# Revit family: Reece_Waste_Mizu_Drift_Tile Insert Waste
name_source: partatom
category: Plumbing Fixtures
revit_build: Autodesk Revit 2018 (Build: 20190510_1515(x64)
units: mm (PartAtom-declared; Revit-internal decimal feet)

## family parameters
Cut with Voids When Loaded = No
Host = Face
Part Type = Normal
Room Calculation Point = Yes
Round Connector Dimension = Use Diameter
Shared = Yes

## types (1)
- 100mm_Chrome
    CW Connection = No
    CWFU = 0
    Default Elevation = 1000 mm  [stored 3.28084 ft]
    Description = Mizu Drift Tile Insert Waste 100mm Chrome
    Disclaimer = THIS FILE IS THE PROPERTY OF THE REECE GROUP. IT MAY NOT BE REPRODUCED, REVERSE-ENGINEERED OR MODIFIED. ANY REPUBLICATION, TRANSMISSION OR DISTRIBUTION FOR THE PURPOSE OF COMMERCIALLY EXPLOITING THE FILES IS PROHIBITED.
    HW Connection = No
    HWFU = 0
    Keynote = Product #202209, Reece_Waste_Mizu_Drift_Tile Insert Waste - 100mm_Chrome
    Manufacturer = Mizu
    Model = Drift
    Reece_Detail_Disclaimer = THIS FILE IS THE PROPERTY OF THE REECE GROUP. IT MAY NOT BE REPRODUCED, REVERSE-ENGINEERED OR MODIFIED. ANY REPUBLICATION, TRANSMISSION OR DISTRIBUTION FOR THE PURPOSE OF COMMERCIALLY EXPLOITING THE FILES IS PROHIBITED.
    Reece_Drain_Offset = 10 mm  [stored 0.0328084 ft]
    Reece_Material_Main = Reece_Brass_Chrome
    Reece_Material_Secondary = <By Category>
    Reece_Overall_Height = 37 mm  [stored 0.121391 ft]
    Reece_Overall_Length = 120 mm  [stored 0.393701 ft]
    Reece_Overall_Width = 120 mm  [stored 0.393701 ft]
    Reece_Product_Brand = Mizu
    Reece_Product_Description = Mizu Drift Tile Insert Waste 100mm Chrome
    Reece_Product_Mount = Floor Inset
    Reece_Product_Number = 202209
    Reece_Product_Sub Brand = Drift
    Reece_Product_Type = Waste
    Reece_Product_Web Page = https://www.reece.com.au
    Reece_Waste_Outlet = 102 mm  [stored 0.334646 ft]
    Type Comments = Waste
    URL = https://www.reece.com.au
    Vent Connection = No
    WFU = 0
    Waste Connection = No

note: [stored X ft] marks values corroborated as IEEE doubles in the binary element streams (Revit-internal decimal feet)

## geometry (parser evidence)
native form markers: Sweep x2
no freeform markers — native parametric forms only
